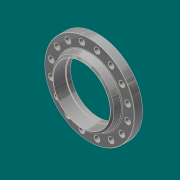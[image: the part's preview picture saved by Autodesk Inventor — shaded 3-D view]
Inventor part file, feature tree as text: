
AUTODESK INVENTOR PART (.ipt)
format: ipt  version: 2017.3 (Build 213257000, 257)  size: 254,976 bytes
history: native  units: in
note: dims shown in document units (in); Inventor stores cm internally (conversion verified against a paired STEP export)
features: chamfer x3, sketch x3, revolve x1, hole x1, pattern_circular x1, extrude x1, fillet x1
ambient origin geometry x8: Origin, YZ Plane, XZ Plane, XY Plane, X Axis, Y Axis, Z Axis, Center Point
bodies: Solid1 (feature_tree)
feature tree (11):
  revolve  "Revolution1"  [1 undecoded]
  hole  "Hole1"  [1 undecoded]
  chamfer  "Chamfer1"  Distance=14.0in
  pattern_circular  "Circular Pattern1"  [2 undecoded]
  chamfer  "Chamfer2"  Distance=14.9in
  extrude  "Extrusion1"  Depth=0.0312in
  fillet  "Fillet1"  Radius=0.4375in
  chamfer  "Chamfer3"  Distance=0.2in
  sketch  "Sketch1"  dims[d0=3.75in d1=20.5in]
  sketch  "Sketch2"  dims[d2=2.0in d3=15.0in]
  sketch  "Sketch3"  dims[d4=0.0625in d5=14.0in d6=13.0in d7=14.9in d8=0.2577in d9=0.4375in d10=0.2in d11=90.0deg d12=17.75in d13=0.0773in d14=1.25in d15=0.75in d16=0.375in d17=0.25in d18=0.5635in d19=1.0in d20=0.8108in d21=0.0625in d22=0.125in d23=45.0deg d24=6.2992in d25=360.0deg d27=0.0625in d28=0.125in d29=45.0deg d30=12.625in d31=1.0in d32=0.0in d33=0.0312in d34=0.0312in d35=0.125in d36=45.0deg]
note: 4 required parameter values undecoded (feature->parameter linkage not recoverable at this tier; creation-order binding heuristic only, values carry confidence <= 0.55)